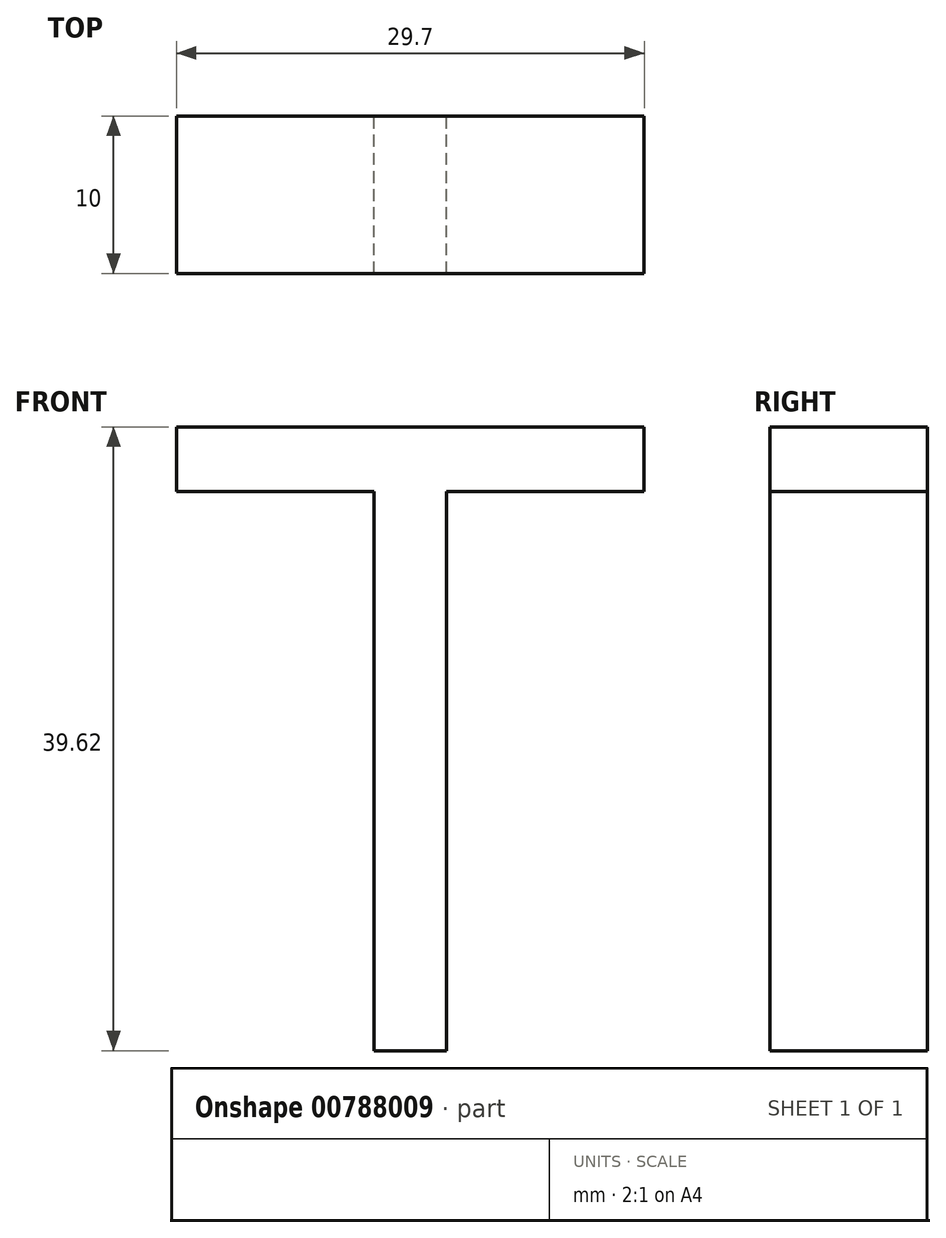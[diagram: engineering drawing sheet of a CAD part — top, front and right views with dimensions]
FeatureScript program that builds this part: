
annotation { "Feature Type Name" : "Feature", "Feature Type Description" : "" }
export const myFeature = defineFeature(function(context is Context, id is Id, definition is map)
    precondition{}
    {
        {
            var Q0;
            Q0=qCreatedBy(makeId("Front.planeOp"),FACE);
            var sketch = newSketch(context, id + "F0", { "sketchPlane" : qUnion([Q0])});
            skText(sketch, "E0", { "text": "T", "fontName": "OpenSans-Regular.ttf"});
            const initialGuessF0  = {"E0": [-0.03378, 0, 1, 0, 0.03996]};
            skSetInitialGuess(sketch, initialGuessF0);
            skSolve(sketch);
        }
        {
            var Q0;
            Q0 = qSketchRegion(id + "F0", true);
            extrude(context, id + "F1", {"entities" : qUnion([Q0]), "depth" : 10 * mm, "offsetDistance" : 25.4 * mm});
        }
    });
